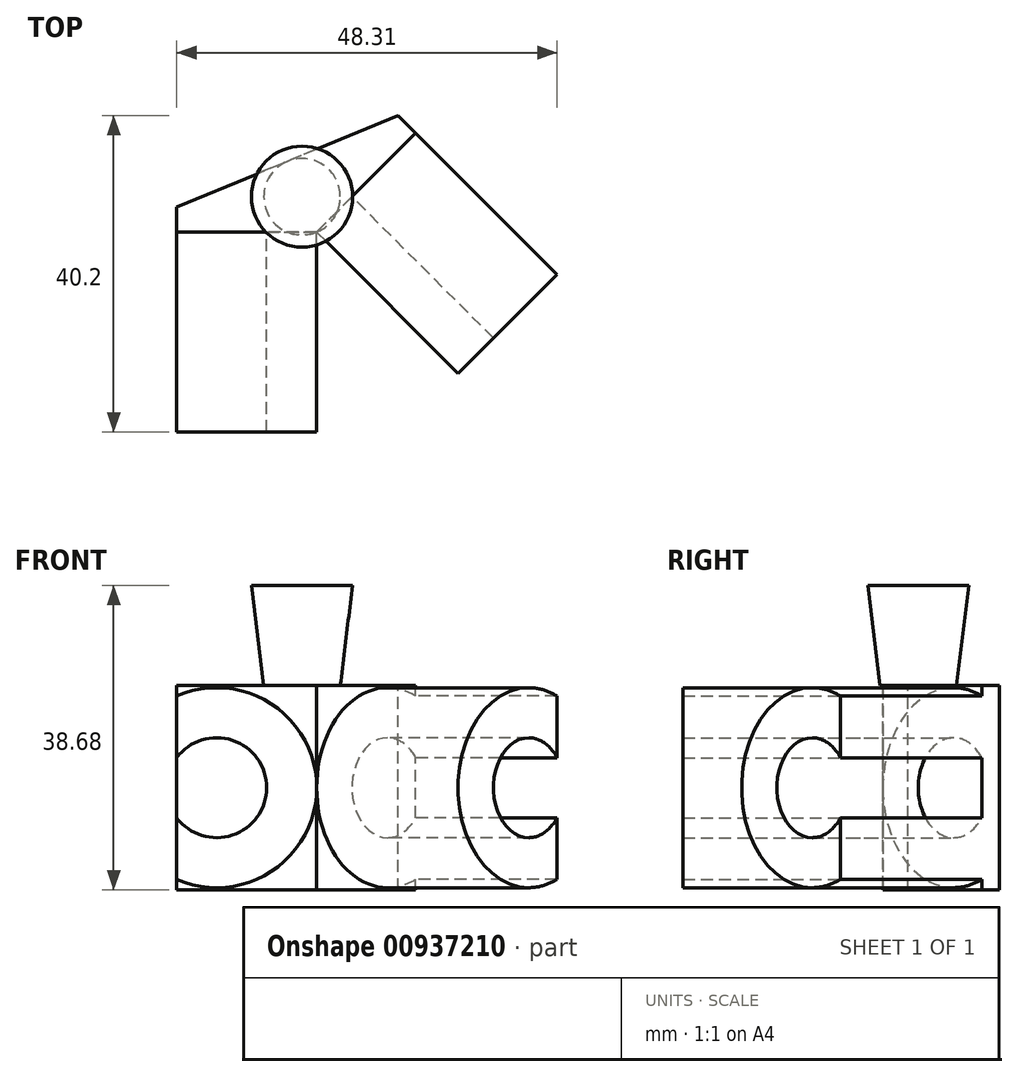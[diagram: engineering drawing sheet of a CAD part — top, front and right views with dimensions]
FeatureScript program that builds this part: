
annotation { "Feature Type Name" : "Feature", "Feature Type Description" : "" }
export const myFeature = defineFeature(function(context is Context, id is Id, definition is map)
    precondition{}
    {
        {
            var Q0;
            Q0=qCreatedBy(makeId("Top.planeOp"),FACE);
            var sketch = newSketch(context, id + "F0", { "sketchPlane" : qUnion([Q0])});
            skLineSegment(sketch, "E0.top", {"start": v(-38.18, -22.13) * mm, "end": v(-12.78, -22.13) * mm});
            skLineSegment(sketch, "E0.right", {"start": v(5.18, -4.17) * mm, "end": v(-12.78, -22.13) * mm});
            skLineSegment(sketch, "E1", {"start": v(5.18, -4.17) * mm, "end": v(-38.18, -22.13) * mm});
            skSolve(sketch);
        }
        {
            var Q0;
            Q0=makeQuery(id+"F0.imprint","IMPRINT",FACE,{"disambiguationData":[TD([[makeQuery(id+"F0.imprint","IMPRINT",EDGE,{"derivedFrom":sQuery(id+"F0.wireOp",EDGE,"E0.top")}),1.0]])]});
            extrude(context, id + "F1", {"entities" : qUnion([Q0]), "depth" : 25.98 * mm, "offsetDistance" : 25.4 * mm});
        }
        {
            var Q0;
            Q0=makeQuery(id+"F1.opExtrude","SWEPT_FACE",FACE,{"disambiguationData":[OSD([sQuery(id+"F0.wireOp",EDGE,"E0.right")])]});
            var sketch = newSketch(context, id + "F2", { "sketchPlane" : qUnion([Q0])});
            skLineSegment(sketch, "E2", {"start": v(-24.7, 25.98) * mm, "end": v(0.7, 0) * mm, "construction": true});
            skLineSegment(sketch, "E3", {"start": v(0.7, 0) * mm, "end": v(0.7, 25.98) * mm, "construction": true});
            skLineSegment(sketch, "E4", {"start": v(0.7, 25.98) * mm, "end": v(-24.7, 0) * mm, "construction": true});
            skCircle(sketch, "E5", {"center": v(-12, 13) * mm, "radius": 12.7 * mm});
            skCircle(sketch, "E6", {"center": v(-12, 13) * mm, "radius": 6.35 * mm});
            skSolve(sketch);
        }
        {
            var Q0;
            Q0 = qSketchRegion(id + "F2", true);
            extrude(context, id + "F3", {"entities" : qUnion([Q0]), "operationType" : NewBodyOperationType.ADD, "depth" : 25.4 * mm, "offsetDistance" : 25.4 * mm});
        }
        {
            var Q0;
            Q0=makeQuery(id+"F1.opExtrude","SWEPT_FACE",FACE,{"disambiguationData":[OSD([sQuery(id+"F0.wireOp",EDGE,"E0.top")])]});
            var sketch = newSketch(context, id + "F4", { "sketchPlane" : qUnion([Q0])});
            skLineSegment(sketch, "E7", {"start": v(-12.78, 0) * mm, "end": v(-38.18, 25.98) * mm, "construction": true});
            skLineSegment(sketch, "E8", {"start": v(-38.18, 25.98) * mm, "end": v(-12.78, 25.98) * mm, "construction": true});
            skLineSegment(sketch, "E9", {"start": v(-12.78, 25.98) * mm, "end": v(-38.18, 0) * mm, "construction": true});
            skCircle(sketch, "E10", {"center": v(-25.48, 13) * mm, "radius": 12.7 * mm});
            skCircle(sketch, "E11", {"center": v(-25.48, 13) * mm, "radius": 6.35 * mm});
            skSolve(sketch);
        }
        {
            var Q0;
            Q0 = qSketchRegion(id + "F4", true);
            extrude(context, id + "F5", {"entities" : qUnion([Q0]), "operationType" : NewBodyOperationType.ADD, "depth" : 25.4 * mm, "offsetDistance" : 25.4 * mm});
        }
        {
            var Q0;
            Q0=makeQuery(id+"F0.imprint","IMPRINT",FACE,{"disambiguationData":[TD([[makeQuery(id+"F0.imprint","IMPRINT",EDGE,{"derivedFrom":sQuery(id+"F0.wireOp",EDGE,"E0.top")}),1.0]])]});
            var sketch = newSketch(context, id + "F6", { "sketchPlane" : qUnion([Q0])});
            skLineSegment(sketch, "E12.bottom", {"start": v(-30.56, -12.93) * mm, "end": v(-52.9, -12.93) * mm});
            skLineSegment(sketch, "E12.top", {"start": v(-30.56, -49.15) * mm, "end": v(-52.9, -49.15) * mm});
            skLineSegment(sketch, "E12.left", {"start": v(-30.56, -12.93) * mm, "end": v(-30.56, -49.15) * mm});
            skLineSegment(sketch, "E12.right", {"start": v(-52.9, -12.93) * mm, "end": v(-52.9, -49.15) * mm});
            skLineSegment(sketch, "E13", {"start": v(-16.5, -13.15) * mm, "end": v(0, -53) * mm, "construction": true});
            skLineSegment(sketch, "E14.MirrorCS", {"start": v(9.08, 12.74) * mm, "end": v(34.69, -12.86) * mm});
            skLineSegment(sketch, "E15.MirrorCS", {"start": v(-6.72, -3.06) * mm, "end": v(18.89, -28.66) * mm});
            skLineSegment(sketch, "E16.MirrorCS", {"start": v(-6.72, -3.06) * mm, "end": v(9.08, 12.74) * mm});
            skLineSegment(sketch, "E17.MirrorCS", {"start": v(18.89, -28.66) * mm, "end": v(34.69, -12.86) * mm});
            skSolve(sketch);
        }
        {
            var Q0;
            Q0=makeQuery(id+"F1.opExtrude","CAP_FACE",FACE,{"disambiguationData":[OSD([sQuery(id+"F0.wireOp",EDGE,"E0.top"),sQuery(id+"F0.wireOp",EDGE,"E0.right"),sQuery(id+"F0.wireOp",EDGE,"E1")])],"isStart":false});
            var sketch = newSketch(context, id + "F7", { "sketchPlane" : qUnion([Q0])});
            skLineSegment(sketch, "E18", {"start": v(-12.78, -22.13) * mm, "end": v(-16.5, -13.15) * mm, "construction": true});
            skPoint(sketch, "E18.endSnap0", {"position": v(-16.5, -13.15) * mm});
            skCircle(sketch, "E19", {"center": v(-14.64, -17.64) * mm, "radius": 4.86 * mm});
            skSolve(sketch);
        }
        {
            var Q0;
            Q0 = qSketchRegion(id + "F7", true);
            extrude(context, id + "F8", {"entities" : qUnion([Q0]), "operationType" : NewBodyOperationType.ADD, "depth" : 12.7 * mm, "offsetDistance" : 25.4 * mm, "hasDraft" : true, "draftAngle" : 7 * degree});
        }
        {
            var Q0;
            Q0 = qSketchRegion(id + "F6", true);
            extrude(context, id + "F9", {"entities" : qUnion([Q0]), "operationType" : NewBodyOperationType.REMOVE, "endBound" : BoundingType.THROUGH_ALL, "depth" : 25.4 * mm, "offsetDistance" : 25.4 * mm});
        }
    });
